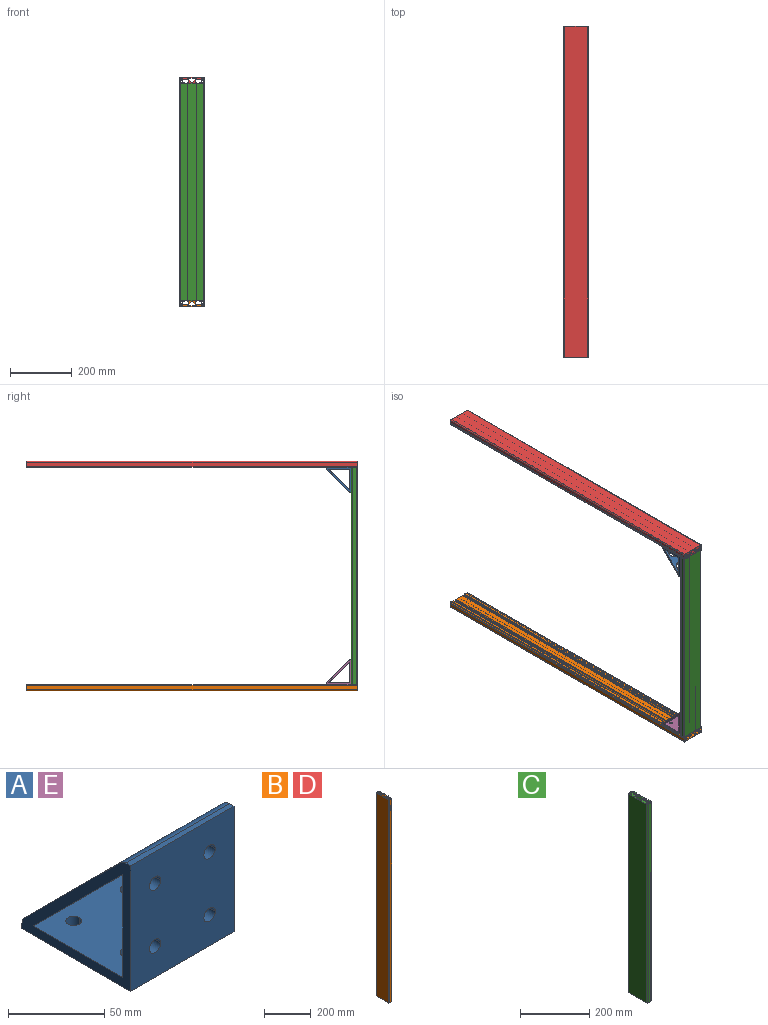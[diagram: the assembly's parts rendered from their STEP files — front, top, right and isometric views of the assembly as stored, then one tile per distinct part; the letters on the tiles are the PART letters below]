
ASSEMBLY  parts=5 mates=10
PART A: 44 faces, bbox 76x80x80 mm
  f0: cylinder r=10mm len=20mm, axis (0,0,-1), area 81.2mm2, adj f1,f3,f28
  f1: cylinder r=10mm len=20mm, axis (0,-1,0), area 81.2mm2, adj f0,f2,f28
  f2: cylinder r=10mm len=20mm, axis (0,0,-1), area 206.7mm2, adj f1,f3,f4
  f3: cylinder r=10mm len=20mm, axis (0,-1,0), area 206.7mm2, adj f0,f2,f4
  f4: plane 76x70.49mm, normal (0,0.71,0.71), area 5119.2mm2, adj f2,f3,f5,f10,f11,f29,f32,f33
  f5: cylinder r=6mm len=76mm, axis (1,0,0), area 358.1mm2, adj f4,f6,f11,f29
  f6: plane 76x3.51mm, normal (0,1,0), area 267.1mm2, adj f5,f7,f11,f29
  f7: plane 80x76mm, normal (0,0,-1), area 5863.6mm2, adj f6,f8,f11,f20,f21,f22,f23,f24
  f8: plane 80x76mm, normal (0,-1,0), area 5863.6mm2, adj f7,f9,f11,f13,f14,f15,f16,f17
  f9: plane 76x3.51mm, normal (0,0,1), area 267.1mm2, adj f8,f10,f11,f29
  f10: cylinder r=6mm len=76mm, axis (1,0,0), area 358.1mm2, adj f4,f9,f11,f29
  f11: plane 80x80mm, normal (1,0,0), area 1514.4mm2, adj f4,f5,f6,f7,f8,f9,f10,f12
  f12: plane 76x65.51mm, normal (0,1,0), area 4762.7mm2, adj f11,f13,f14,f15,f16,f17,f18,f19
  f13: cylinder r=4.15mm len=8.3mm, axis (0,1,0), area 78.2mm2, adj f8,f12,f14
  f14: cylinder r=4.15mm len=8.3mm, axis (0,1,0), area 78.2mm2, adj f8,f12,f13
  f15: cylinder r=4.15mm len=8.3mm, axis (0,1,0), area 78.2mm2, adj f8,f12,f16
  f16: cylinder r=4.15mm len=8.3mm, axis (0,1,0), area 78.2mm2, adj f8,f12,f15
  f17: cylinder r=4.15mm len=8.3mm, axis (0,1,0), area 78.2mm2, adj f8,f12,f18
  f18: cylinder r=4.15mm len=8.3mm, axis (0,1,0), area 78.2mm2, adj f8,f12,f17
  f19: plane 76x65.51mm, normal (0,0,1), area 4762.7mm2, adj f11,f12,f20,f21,f22,f23,f24,f25
  f20: cylinder r=4.15mm len=8.3mm, axis (0,0,1), area 78.2mm2, adj f7,f19,f21
  f21: cylinder r=4.15mm len=8.3mm, axis (0,0,1), area 78.2mm2, adj f7,f19,f20
  f22: cylinder r=4.15mm len=8.3mm, axis (0,0,1), area 78.2mm2, adj f7,f19,f23
  f23: cylinder r=4.15mm len=8.3mm, axis (0,0,1), area 78.2mm2, adj f7,f19,f22
  f24: cylinder r=4.15mm len=8.3mm, axis (0,0,1), area 78.2mm2, adj f7,f19,f25
  f25: cylinder r=4.15mm len=8.3mm, axis (0,0,1), area 78.2mm2, adj f7,f19,f24
  f26: cylinder r=4.15mm len=8.3mm, axis (0,0,1), area 78.2mm2, adj f7,f19,f27
  f27: cylinder r=4.15mm len=8.3mm, axis (0,0,1), area 78.2mm2, adj f7,f19,f26
  f28: plane 76x65.51mm, normal (0,-0.71,-0.71), area 4983.9mm2, adj f0,f1,f11,f12,f19,f29,f30,f31
  f29: plane 80x80mm, normal (-1,0,0), area 1514.4mm2, adj f4,f5,f6,f7,f8,f9,f10,f12
  f30: cylinder r=10mm len=20mm, axis (0,-1,0), area 81.2mm2, adj f28,f31,f33
  f31: cylinder r=10mm len=20mm, axis (0,0,-1), area 81.2mm2, adj f28,f30,f32
  f32: cylinder r=10mm len=20mm, axis (0,-1,0), area 206.7mm2, adj f4,f31,f33
  f33: cylinder r=10mm len=20mm, axis (0,0,-1), area 206.7mm2, adj f4,f30,f32
  f34: cylinder r=10mm len=20mm, axis (0,0,-1), area 81.2mm2, adj f28,f35,f37
  f35: cylinder r=10mm len=20mm, axis (0,-1,0), area 81.2mm2, adj f28,f34,f36
  f36: cylinder r=10mm len=20mm, axis (0,0,-1), area 206.7mm2, adj f4,f35,f37
  f37: cylinder r=10mm len=20mm, axis (0,-1,0), area 206.7mm2, adj f4,f34,f36
  f38: cylinder r=10mm len=20mm, axis (0,-1,0), area 81.2mm2, adj f28,f39,f41
  f39: cylinder r=10mm len=20mm, axis (0,0,-1), area 81.2mm2, adj f28,f38,f40
  f40: cylinder r=10mm len=20mm, axis (0,-1,0), area 206.7mm2, adj f4,f39,f41
  f41: cylinder r=10mm len=20mm, axis (0,0,-1), area 206.7mm2, adj f4,f38,f40
  f42: cylinder r=4.15mm len=8.3mm, axis (0,1,0), area 78.2mm2, adj f8,f12,f43
  f43: cylinder r=4.15mm len=8.3mm, axis (0,1,0), area 78.2mm2, adj f8,f12,f42
PART B: 84 faces, bbox 20x80x1066.8 mm
  f0: plane 1066.8x73.65mm, normal (-1,0,0), area 78570.7mm2, adj f1,f10,f82,f83
  f1: cylinder r=3.17mm len=1066.8mm, axis (0,0,-1), area 5319.8mm2, adj f0,f2,f82,f83
  f2: plane 1066.8x13.65mm, normal (0,-1,0), area 14562.7mm2, adj f1,f3,f82,f83
  f3: cylinder r=3.17mm len=1066.8mm, axis (0,0,-1), area 5319.8mm2, adj f2,f4,f82,f83
  f4: plane 1066.8x11.18mm, normal (1,0,0), area 11928.2mm2, adj f3,f5,f82,f83
  f5: cylinder r=1.58mm len=1066.8mm, axis (0,0,-1), area 2654.5mm2, adj f4,f6,f82,f83
  f6: plane 1066.8x0.9mm, normal (0,1,0), area 965.2mm2, adj f5,f7,f82,f83
  f7: cylinder r=1.57mm len=1066.8mm, axis (0,0,-1), area 2638.6mm2, adj f6,f8,f82,f83
  f8: plane 1066.8x1.26mm, normal (-1,0,0), area 1348.4mm2, adj f7,f28,f82,f83
  f9: plane 1066.8x13.65mm, normal (0,1,0), area 14562.7mm2, adj f10,f11,f82,f83
  f10: cylinder r=3.17mm len=1066.8mm, axis (0,0,-1), area 5319.8mm2, adj f0,f9,f82,f83
  f11: cylinder r=3.17mm len=1066.8mm, axis (0,0,-1), area 5319.8mm2, adj f9,f12,f82,f83
  f12: plane 1066.8x11.18mm, normal (1,0,0), area 11928.2mm2, adj f11,f13,f82,f83
  f13: cylinder r=1.58mm len=1066.8mm, axis (0,0,-1), area 2654.5mm2, adj f12,f14,f82,f83
  f14: plane 1066.8x0.9mm, normal (0,-1,0), area 965.2mm2, adj f13,f15,f82,f83
  f15: cylinder r=1.57mm len=1066.8mm, axis (0,0,-1), area 2638.6mm2, adj f14,f16,f82,f83
  f16: plane 1066.8x1.26mm, normal (-1,0,0), area 1348.4mm2, adj f15,f31,f82,f83
  f17: plane 1066.8x1.26mm, normal (-1,0,0), area 1348.4mm2, adj f18,f45,f82,f83
  f18: cylinder r=1.57mm len=1066.8mm, axis (0,0,-1), area 2638.6mm2, adj f17,f19,f82,f83
  f19: plane 1066.8x0.9mm, normal (0,1,0), area 965.2mm2, adj f18,f20,f82,f83
  f20: cylinder r=1.58mm len=1066.8mm, axis (0,0,-1), area 2654.5mm2, adj f19,f21,f82,f83
  f21: plane 1066.8x28.71mm, normal (1,0,0), area 30629.7mm2, adj f20,f22,f82,f83
  f22: cylinder r=1.58mm len=1066.8mm, axis (0,0,-1), area 2654.5mm2, adj f21,f23,f82,f83
  f23: plane 1066.8x0.9mm, normal (0,-1,0), area 965.2mm2, adj f22,f24,f82,f83
  f24: cylinder r=1.57mm len=1066.8mm, axis (0,0,-1), area 2638.6mm2, adj f23,f25,f82,f83
  f25: plane 1066.8x1.26mm, normal (-1,0,0), area 1348.4mm2, adj f24,f46,f82,f83
  f26: plane 1066.8x12.64mm, normal (-0.71,-0.71,0), area 19069.4mm2, adj f27,f75,f82,f83
  f27: cylinder r=0.63mm len=1066.8mm, axis (0,0,-1), area 532mm2, adj f26,f79,f82,f83
  f28: plane 1066.8x0.47mm, normal (0,-1,0), area 500.2mm2, adj f8,f29,f82,f83
  f29: plane 1066.8x2.12mm, normal (-1,0,0), area 2258mm2, adj f28,f30,f82,f83
  f30: cylinder r=1.27mm len=1066.8mm, axis (0,0,-1), area 2127.9mm2, adj f29,f57,f82,f83
  f31: plane 1066.8x0.47mm, normal (0,1,0), area 500.2mm2, adj f16,f32,f82,f83
  f32: plane 1066.8x2.12mm, normal (-1,0,0), area 2258mm2, adj f31,f33,f82,f83
  f33: cylinder r=1.27mm len=1066.8mm, axis (0,0,-1), area 2127.9mm2, adj f32,f34,f82,f83
  f34: plane 1066.8x2.42mm, normal (0,-1,0), area 2584.2mm2, adj f33,f35,f82,f83
  f35: cylinder r=0.8mm len=1066.8mm, axis (0,0,-1), area 670.3mm2, adj f34,f36,f82,f83
  f36: plane 1066.8x3.06mm, normal (0.71,-0.71,0), area 4610.9mm2, adj f35,f37,f82,f83
  f37: cylinder r=4.75mm len=1066.8mm, axis (0,0,-1), area 3979.3mm2, adj f36,f38,f82,f83
  f38: plane 1066.8x7.27mm, normal (1,0,0), area 7758.3mm2, adj f37,f39,f82,f83
  f39: cylinder r=4.75mm len=1066.8mm, axis (0,0,-1), area 3979.3mm2, adj f38,f40,f82,f83
  f40: plane 1066.8x3.06mm, normal (0.71,0.71,0), area 4610.9mm2, adj f39,f41,f82,f83
  f41: cylinder r=0.8mm len=1066.8mm, axis (0,0,-1), area 670.3mm2, adj f40,f42,f82,f83
  f42: plane 1066.8x2.42mm, normal (0,1,0), area 2584.2mm2, adj f41,f43,f82,f83
  f43: cylinder r=1.27mm len=1066.8mm, axis (0,0,-1), area 2127.9mm2, adj f42,f44,f82,f83
  f44: plane 1066.8x2.12mm, normal (-1,0,0), area 2258mm2, adj f43,f45,f82,f83
  f45: plane 1066.8x0.47mm, normal (0,-1,0), area 500.2mm2, adj f17,f44,f82,f83
  f46: plane 1066.8x0.47mm, normal (0,1,0), area 500.2mm2, adj f25,f47,f82,f83
  f47: plane 1066.8x2.12mm, normal (-1,0,0), area 2258mm2, adj f46,f48,f82,f83
  f48: cylinder r=1.27mm len=1066.8mm, axis (0,0,-1), area 2127.9mm2, adj f47,f49,f82,f83
  f49: plane 1066.8x2.42mm, normal (0,-1,0), area 2584.2mm2, adj f48,f50,f82,f83
  f50: cylinder r=0.8mm len=1066.8mm, axis (0,0,-1), area 670.3mm2, adj f49,f51,f82,f83
  f51: plane 1066.8x3.06mm, normal (0.71,-0.71,0), area 4610.9mm2, adj f50,f52,f82,f83
  f52: cylinder r=4.75mm len=1066.8mm, axis (0,0,-1), area 3979.3mm2, adj f51,f53,f82,f83
  f53: plane 1066.8x7.27mm, normal (1,0,0), area 7758.3mm2, adj f52,f54,f82,f83
  f54: cylinder r=4.75mm len=1066.8mm, axis (0,0,-1), area 3979.3mm2, adj f53,f55,f82,f83
  f55: plane 1066.8x3.06mm, normal (0.71,0.71,0), area 4610.9mm2, adj f54,f56,f82,f83
  f56: cylinder r=0.8mm len=1066.8mm, axis (0,0,-1), area 670.3mm2, adj f55,f57,f82,f83
  f57: plane 1066.8x2.42mm, normal (0,1,0), area 2584.2mm2, adj f30,f56,f82,f83
  f58: plane 1066.8x4.51mm, normal (1,0,0), area 4811.5mm2, adj f59,f65,f82,f83
  f59: cylinder r=1.27mm len=1066.8mm, axis (0,0,-1), area 2127.9mm2, adj f58,f60,f82,f83
  f60: plane 1066.8x4.49mm, normal (0,-1,0), area 4784.5mm2, adj f59,f61,f82,f83
  f61: cylinder r=0.63mm len=1066.8mm, axis (0,0,-1), area 1064mm2, adj f60,f62,f82,f83
  f62: plane 1066.8x2.99mm, normal (-1,0,0), area 3185.9mm2, adj f61,f63,f82,f83
  f63: cylinder r=2.79mm len=1066.8mm, axis (0,0,-1), area 4681.4mm2, adj f62,f64,f82,f83
  f64: plane 1066.8x2.96mm, normal (0,1,0), area 3158.9mm2, adj f63,f65,f82,f83
  f65: cylinder r=0.63mm len=1066.8mm, axis (0,0,-1), area 1064mm2, adj f58,f64,f82,f83
  f66: cylinder r=1.27mm len=1066.8mm, axis (0,0,-1), area 2127.9mm2, adj f67,f73,f82,f83
  f67: plane 1066.8x4.49mm, normal (0,1,0), area 4784.5mm2, adj f66,f68,f82,f83
  f68: cylinder r=0.63mm len=1066.8mm, axis (0,0,-1), area 1064mm2, adj f67,f69,f82,f83
  f69: plane 1066.8x2.99mm, normal (-1,0,0), area 3185.9mm2, adj f68,f70,f82,f83
  f70: cylinder r=2.79mm len=1066.8mm, axis (0,0,-1), area 4681.4mm2, adj f69,f71,f82,f83
  f71: plane 1066.8x2.96mm, normal (0,-1,0), area 3158.9mm2, adj f70,f72,f82,f83
  f72: cylinder r=0.63mm len=1066.8mm, axis (0,0,-1), area 1064mm2, adj f71,f73,f82,f83
  f73: plane 1066.8x4.51mm, normal (1,0,0), area 4811.5mm2, adj f66,f72,f82,f83
  f74: plane 1066.8x26.9mm, normal (1,0,0), area 28697.3mm2, adj f75,f76,f82,f83
  f75: cylinder r=0.63mm len=1066.8mm, axis (0,0,-1), area 1595.9mm2, adj f26,f74,f82,f83
  f76: cylinder r=0.63mm len=1066.8mm, axis (0,0,-1), area 1595.9mm2, adj f74,f77,f82,f83
  f77: plane 1066.8x12.64mm, normal (-0.71,0.71,0), area 19069.4mm2, adj f76,f78,f82,f83
  f78: cylinder r=0.63mm len=1066.8mm, axis (0,0,-1), area 532mm2, adj f77,f79,f82,f83
  f79: plane 1066.8x1.62mm, normal (-1,0,0), area 1729.1mm2, adj f27,f78,f82,f83
  f80: cylinder r=3.4mm len=1066.8mm, axis (0,0,-1), area 22789.9mm2, adj f82,f83
  f81: cylinder r=3.4mm len=1066.8mm, axis (0,0,-1), area 22789.9mm2, adj f82,f83
  f82: plane 80x20mm, normal (0,0,1), area 850.5mm2, adj f0,f1,f2,f3,f4,f5,f6,f7
  f83: plane 80x20mm, normal (0,0,-1), area 850.5mm2, adj f0,f1,f2,f3,f4,f5,f6,f7
PART C: 84 faces, bbox 20x80x701 mm
  f0: plane 701.04x73.65mm, normal (-1,0,0), area 51632.2mm2, adj f1,f10,f82,f83
  f1: cylinder r=3.17mm len=701.04mm, axis (0,0,-1), area 3495.8mm2, adj f0,f2,f82,f83
  f2: plane 701.04x13.65mm, normal (0,-1,0), area 9569.8mm2, adj f1,f3,f82,f83
  f3: cylinder r=3.17mm len=701.04mm, axis (0,0,-1), area 3495.8mm2, adj f2,f4,f82,f83
  f4: plane 701.04x11.18mm, normal (1,0,0), area 7838.5mm2, adj f3,f5,f82,f83
  f5: cylinder r=1.58mm len=701.04mm, axis (0,0,-1), area 1744.4mm2, adj f4,f6,f82,f83
  f6: plane 701.04x0.9mm, normal (0,1,0), area 634.3mm2, adj f5,f7,f82,f83
  f7: cylinder r=1.57mm len=701.04mm, axis (0,0,-1), area 1733.9mm2, adj f6,f8,f82,f83
  f8: plane 701.04x1.26mm, normal (-1,0,0), area 886.1mm2, adj f7,f28,f82,f83
  f9: plane 701.04x13.65mm, normal (0,1,0), area 9569.8mm2, adj f10,f11,f82,f83
  f10: cylinder r=3.17mm len=701.04mm, axis (0,0,-1), area 3495.8mm2, adj f0,f9,f82,f83
  f11: cylinder r=3.17mm len=701.04mm, axis (0,0,-1), area 3495.8mm2, adj f9,f12,f82,f83
  f12: plane 701.04x11.18mm, normal (1,0,0), area 7838.5mm2, adj f11,f13,f82,f83
  f13: cylinder r=1.58mm len=701.04mm, axis (0,0,-1), area 1744.4mm2, adj f12,f14,f82,f83
  f14: plane 701.04x0.9mm, normal (0,-1,0), area 634.3mm2, adj f13,f15,f82,f83
  f15: cylinder r=1.57mm len=701.04mm, axis (0,0,-1), area 1733.9mm2, adj f14,f16,f82,f83
  f16: plane 701.04x1.26mm, normal (-1,0,0), area 886.1mm2, adj f15,f31,f82,f83
  f17: plane 701.04x1.26mm, normal (-1,0,0), area 886.1mm2, adj f18,f45,f82,f83
  f18: cylinder r=1.57mm len=701.04mm, axis (0,0,-1), area 1733.9mm2, adj f17,f19,f82,f83
  f19: plane 701.04x0.9mm, normal (0,1,0), area 634.3mm2, adj f18,f20,f82,f83
  f20: cylinder r=1.58mm len=701.04mm, axis (0,0,-1), area 1744.4mm2, adj f19,f21,f82,f83
  f21: plane 701.04x28.71mm, normal (1,0,0), area 20128.1mm2, adj f20,f22,f82,f83
  f22: cylinder r=1.58mm len=701.04mm, axis (0,0,-1), area 1744.4mm2, adj f21,f23,f82,f83
  f23: plane 701.04x0.9mm, normal (0,-1,0), area 634.3mm2, adj f22,f24,f82,f83
  f24: cylinder r=1.57mm len=701.04mm, axis (0,0,-1), area 1733.9mm2, adj f23,f25,f82,f83
  f25: plane 701.04x1.26mm, normal (-1,0,0), area 886.1mm2, adj f24,f46,f82,f83
  f26: plane 701.04x12.64mm, normal (-0.71,-0.71,0), area 12531.3mm2, adj f27,f75,f82,f83
  f27: cylinder r=0.63mm len=701.04mm, axis (0,0,-1), area 349.6mm2, adj f26,f79,f82,f83
  f28: plane 701.04x0.47mm, normal (0,-1,0), area 328.7mm2, adj f8,f29,f82,f83
  f29: plane 701.04x2.12mm, normal (-1,0,0), area 1483.8mm2, adj f28,f30,f82,f83
  f30: cylinder r=1.27mm len=701.04mm, axis (0,0,-1), area 1398.3mm2, adj f29,f57,f82,f83
  f31: plane 701.04x0.47mm, normal (0,1,0), area 328.7mm2, adj f16,f32,f82,f83
  f32: plane 701.04x2.12mm, normal (-1,0,0), area 1483.8mm2, adj f31,f33,f82,f83
  f33: cylinder r=1.27mm len=701.04mm, axis (0,0,-1), area 1398.3mm2, adj f32,f34,f82,f83
  f34: plane 701.04x2.42mm, normal (0,-1,0), area 1698.2mm2, adj f33,f35,f82,f83
  f35: cylinder r=0.8mm len=701.04mm, axis (0,0,-1), area 440.5mm2, adj f34,f36,f82,f83
  f36: plane 701.04x3.06mm, normal (0.71,-0.71,0), area 3030mm2, adj f35,f37,f82,f83
  f37: cylinder r=4.75mm len=701.04mm, axis (0,0,-1), area 2615mm2, adj f36,f38,f82,f83
  f38: plane 701.04x7.27mm, normal (1,0,0), area 5098.3mm2, adj f37,f39,f82,f83
  f39: cylinder r=4.75mm len=701.04mm, axis (0,0,-1), area 2615mm2, adj f38,f40,f82,f83
  f40: plane 701.04x3.06mm, normal (0.71,0.71,0), area 3030mm2, adj f39,f41,f82,f83
  f41: cylinder r=0.8mm len=701.04mm, axis (0,0,-1), area 440.5mm2, adj f40,f42,f82,f83
  f42: plane 701.04x2.42mm, normal (0,1,0), area 1698.2mm2, adj f41,f43,f82,f83
  f43: cylinder r=1.27mm len=701.04mm, axis (0,0,-1), area 1398.3mm2, adj f42,f44,f82,f83
  f44: plane 701.04x2.12mm, normal (-1,0,0), area 1483.8mm2, adj f43,f45,f82,f83
  f45: plane 701.04x0.47mm, normal (0,-1,0), area 328.7mm2, adj f17,f44,f82,f83
  f46: plane 701.04x0.47mm, normal (0,1,0), area 328.7mm2, adj f25,f47,f82,f83
  f47: plane 701.04x2.12mm, normal (-1,0,0), area 1483.8mm2, adj f46,f48,f82,f83
  f48: cylinder r=1.27mm len=701.04mm, axis (0,0,-1), area 1398.3mm2, adj f47,f49,f82,f83
  f49: plane 701.04x2.42mm, normal (0,-1,0), area 1698.2mm2, adj f48,f50,f82,f83
  f50: cylinder r=0.8mm len=701.04mm, axis (0,0,-1), area 440.5mm2, adj f49,f51,f82,f83
  f51: plane 701.04x3.06mm, normal (0.71,-0.71,0), area 3030mm2, adj f50,f52,f82,f83
  f52: cylinder r=4.75mm len=701.04mm, axis (0,0,-1), area 2615mm2, adj f51,f53,f82,f83
  f53: plane 701.04x7.27mm, normal (1,0,0), area 5098.3mm2, adj f52,f54,f82,f83
  f54: cylinder r=4.75mm len=701.04mm, axis (0,0,-1), area 2615mm2, adj f53,f55,f82,f83
  f55: plane 701.04x3.06mm, normal (0.71,0.71,0), area 3030mm2, adj f54,f56,f82,f83
  f56: cylinder r=0.8mm len=701.04mm, axis (0,0,-1), area 440.5mm2, adj f55,f57,f82,f83
  f57: plane 701.04x2.42mm, normal (0,1,0), area 1698.2mm2, adj f30,f56,f82,f83
  f58: plane 701.04x4.51mm, normal (1,0,0), area 3161.9mm2, adj f59,f65,f82,f83
  f59: cylinder r=1.27mm len=701.04mm, axis (0,0,-1), area 1398.3mm2, adj f58,f60,f82,f83
  f60: plane 701.04x4.49mm, normal (0,-1,0), area 3144.1mm2, adj f59,f61,f82,f83
  f61: cylinder r=0.63mm len=701.04mm, axis (0,0,-1), area 699.2mm2, adj f60,f62,f82,f83
  f62: plane 701.04x2.99mm, normal (-1,0,0), area 2093.6mm2, adj f61,f63,f82,f83
  f63: cylinder r=2.79mm len=701.04mm, axis (0,0,-1), area 3076.3mm2, adj f62,f64,f82,f83
  f64: plane 701.04x2.96mm, normal (0,1,0), area 2075.8mm2, adj f63,f65,f82,f83
  f65: cylinder r=0.63mm len=701.04mm, axis (0,0,-1), area 699.2mm2, adj f58,f64,f82,f83
  f66: cylinder r=1.27mm len=701.04mm, axis (0,0,-1), area 1398.3mm2, adj f67,f73,f82,f83
  f67: plane 701.04x4.49mm, normal (0,1,0), area 3144.1mm2, adj f66,f68,f82,f83
  f68: cylinder r=0.63mm len=701.04mm, axis (0,0,-1), area 699.2mm2, adj f67,f69,f82,f83
  f69: plane 701.04x2.99mm, normal (-1,0,0), area 2093.6mm2, adj f68,f70,f82,f83
  f70: cylinder r=2.79mm len=701.04mm, axis (0,0,-1), area 3076.3mm2, adj f69,f71,f82,f83
  f71: plane 701.04x2.96mm, normal (0,-1,0), area 2075.8mm2, adj f70,f72,f82,f83
  f72: cylinder r=0.63mm len=701.04mm, axis (0,0,-1), area 699.2mm2, adj f71,f73,f82,f83
  f73: plane 701.04x4.51mm, normal (1,0,0), area 3161.9mm2, adj f66,f72,f82,f83
  f74: plane 701.04x26.9mm, normal (1,0,0), area 18858.2mm2, adj f75,f76,f82,f83
  f75: cylinder r=0.63mm len=701.04mm, axis (0,0,-1), area 1048.8mm2, adj f26,f74,f82,f83
  f76: cylinder r=0.63mm len=701.04mm, axis (0,0,-1), area 1048.8mm2, adj f74,f77,f82,f83
  f77: plane 701.04x12.64mm, normal (-0.71,0.71,0), area 12531.3mm2, adj f76,f78,f82,f83
  f78: cylinder r=0.63mm len=701.04mm, axis (0,0,-1), area 349.6mm2, adj f77,f79,f82,f83
  f79: plane 701.04x1.62mm, normal (-1,0,0), area 1136.3mm2, adj f27,f78,f82,f83
  f80: cylinder r=3.4mm len=701.04mm, axis (0,0,-1), area 14976.2mm2, adj f82,f83
  f81: cylinder r=3.4mm len=701.04mm, axis (0,0,-1), area 14976.2mm2, adj f82,f83
  f82: plane 80x20mm, normal (0,0,1), area 850.5mm2, adj f0,f1,f2,f3,f4,f5,f6,f7
  f83: plane 80x20mm, normal (0,0,-1), area 850.5mm2, adj f0,f1,f2,f3,f4,f5,f6,f7
PART D: same geometry as B
PART E: same geometry as A
PLACE A rot(axis=(0,1,0),180deg) t=(0,-1046.8,721.04)mm
PLACE B rot(axis=(0.58,-0.58,0.58),120deg) t=(0,0,0)mm
PLACE C rot(axis=(0,0,1),90deg) t=(0,-1066.8,20)mm
PLACE D rot(axis=(0.58,0.58,-0.58),120deg) t=(0,0,741.04)mm
PLACE E t=(0,-1046.8,20)mm
MATE planar A.f8 <-> C.f21  axis (0,-1,0) through (0,-1046.8,681.04)mm
MATE planar C.f21 <-> E.f8  axis (0,1,0) through (0,-1046.8,370.52)mm
MATE planar A.f29 <-> E.f11  axis (1,0,0) through (38,-1040.8,715.04)mm
MATE planar D.f21 <-> C.f82  axis (0,0,-1) through (0,-533.4,721.04)mm
MATE planar D.f82 <-> C.f0  axis (0,-1,0) through (0,-1066.8,732.1)mm
MATE planar C.f2 <-> B.f2  axis (1,0,0) through (40,-1056.8,370.52)mm
MATE planar D.f9 <-> C.f2  axis (1,0,0) through (40,-533.4,731.04)mm
MATE planar B.f82 <-> C.f0  axis (0,-1,0) through (0,-1066.8,8.94)mm
MATE planar A.f7 <-> D.f21  axis (0,0,1) through (0,-1006.8,721.04)mm
MATE planar C.f83 <-> B.f21  axis (0,0,-1) through (0,-1057.86,20)mm
